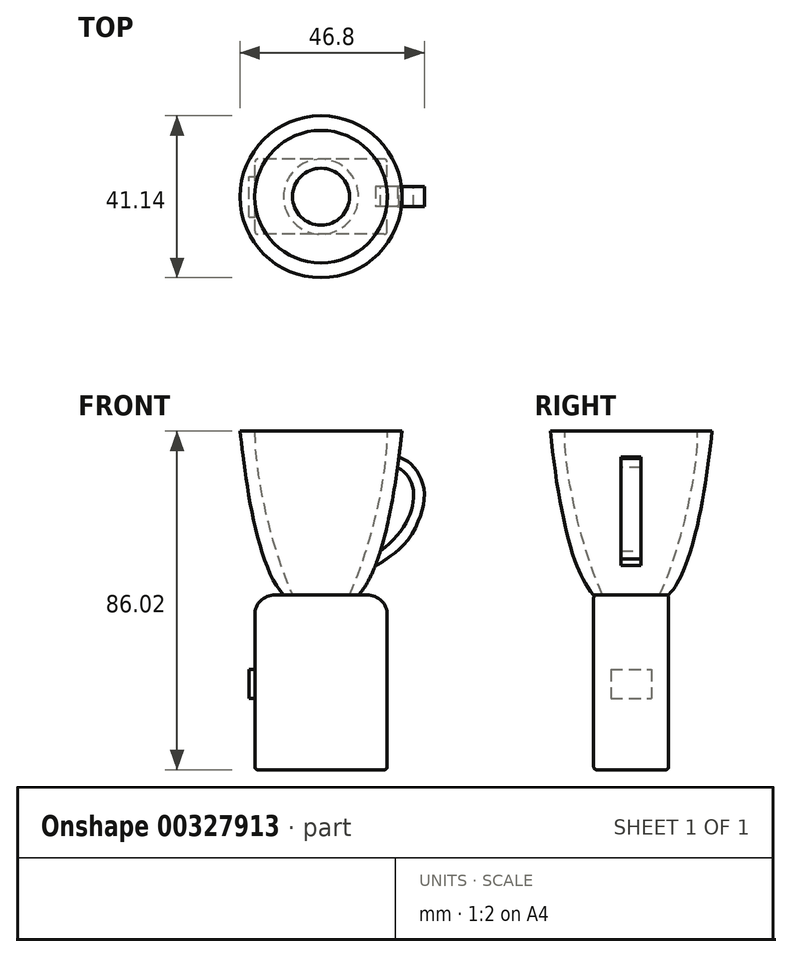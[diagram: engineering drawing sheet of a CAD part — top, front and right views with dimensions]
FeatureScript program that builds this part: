
annotation { "Feature Type Name" : "Feature", "Feature Type Description" : "" }
export const myFeature = defineFeature(function(context is Context, id is Id, definition is map)
    precondition{}
    {
        {
            var Q0;
            Q0=qCreatedBy(makeId("Front.planeOp"),FACE);
            var sketch = newSketch(context, id + "F0", { "sketchPlane" : qUnion([Q0])});
            skLineSegment(sketch, "E0.bottom", {"start": v(11.73, 0) * mm, "end": v(-11.73, 0) * mm});
            skLineSegment(sketch, "E0.top", {"start": v(16.81, -44.43) * mm, "end": v(-16.81, -44.43) * mm});
            skLineSegment(sketch, "E0.left", {"start": v(16.81, -5.08) * mm, "end": v(16.81, -44.43) * mm});
            skLineSegment(sketch, "E0.right", {"start": v(-16.81, -5.08) * mm, "end": v(-16.81, -44.43) * mm});
            skPoint(sketch, "E0.middle", {"position": v(0, -22.22) * mm});
            skLineSegment(sketch, "E1.top", {"start": v(20.57, 41.59) * mm, "end": v(-20.57, 41.59) * mm});
            skPoint(sketch, "E1.middle", {"position": v(0, 20.8) * mm});
            skFitSpline(sketch, "E2", {"points": [v(20.57, 41.59) * mm, v(9.52, 0) * mm], "startDerivative": vector(-3.41, -29.28) * mm, "endDerivative": vector(-21.77, -23.15) * mm});
            skFitSpline(sketch, "E3.MirrorCS", {"points": [v(-20.57, 41.59) * mm, v(-9.52, 0) * mm], "startDerivative": vector(3.41, -29.28) * mm, "endDerivative": vector(21.77, -23.15) * mm});
            skArc(sketch, "E4.filletArc", {"start": v(-11.73, 0) * mm, "mid": v(-15.33, -1.49) * mm, "end": v(-16.81, -5.08) * mm});
            skArc(sketch, "E5.filletArc", {"start": v(16.81, -5.08) * mm, "mid": v(15.33, -1.49) * mm, "end": v(11.73, 0) * mm});
            skLineSegment(sketch, "E6", {"start": v(20.05, 36.32) * mm, "end": v(19.95, 36.34) * mm});
            skPoint(sketch, "E7", {"position": v(19.44, 32.4) * mm});
            skPoint(sketch, "E8", {"position": v(15.09, 11.15) * mm});
            skFitSpline(sketch, "E9", {"points": [v(19.44, 32.4) * mm, v(15.09, 11.15) * mm], "startDerivative": vector(20, -10.29) * mm, "endDerivative": vector(-28.56, -21.1) * mm});
            skLineSegment(sketch, "E10", {"start": v(0, 0) * mm, "end": v(0, 41.59) * mm});
            skFitSpline(sketch, "E11", {"points": [v(-16.84, 41.59) * mm, v(-16.17, 32.06) * mm, v(-7.24, 0) * mm], "startDerivative": vector(-0.17, -23.5) * mm, "endDerivative": vector(23.63, -52.14) * mm});
            skFitSpline(sketch, "E12.0", {"points": [v(20.6, 34.67) * mm, v(21.69, 34.1) * mm, v(23.13, 33) * mm, v(24.53, 31.14) * mm, v(25.57, 29.08) * mm, v(26.2, 26.25) * mm, v(25.98, 22.68) * mm, v(24.89, 19.07) * mm, v(22.33, 14.33) * mm, v(19.2, 11.03) * mm, v(16.6, 9.1) * mm]});
            skLineSegment(sketch, "E13", {"start": v(20.6, 34.67) * mm, "end": v(19.78, 35.04) * mm});
            skFitSpline(sketch, "E14", {"points": [v(16.6, 9.1) * mm, v(13.8, 7.43) * mm], "startDerivative": vector(-2.48, -1.8) * mm, "endDerivative": vector(-3.15, -1.16) * mm});
            skSolve(sketch);
        }
        {
            var Q0;
            Q0=makeQuery(id+"F0.imprint","IMPRINT",FACE,{"disambiguationData":[TD([[makeQuery(id+"F0.imprint","IMPRINT",EDGE,{"derivedFrom":sQuery(id+"F0.wireOp",EDGE,"E0.top")}),-1.0]])]});
            extrude(context, id + "F1", {"entities" : qUnion([Q0]), "endBound" : BoundingType.SYMMETRIC, "depth" : 19.05 * mm});
        }
        {
            var Q0;
            Q0=makeQuery(id+"F1.opExtrude","CAP_EDGE",EDGE,{"disambiguationData":[OSD([sQuery(id+"F0.wireOp",EDGE,"E0.bottom")])],"isStart":false});
            var Q1;
            Q1=makeQuery(id+"F1.opExtrude","CAP_EDGE",EDGE,{"disambiguationData":[OSD([sQuery(id+"F0.wireOp",EDGE,"E0.left")])],"isStart":false});
            var Q2;
            Q2=makeQuery(id+"F1.opExtrude","CAP_EDGE",EDGE,{"disambiguationData":[OSD([sQuery(id+"F0.wireOp",EDGE,"E5.filletArc")])],"isStart":false});
            var Q3;
            Q3=makeQuery(id+"F1.opExtrude","CAP_EDGE",EDGE,{"disambiguationData":[OSD([sQuery(id+"F0.wireOp",EDGE,"E5.filletArc")])],"isStart":true});
            var Q4;
            Q4=makeQuery(id+"F1.opExtrude","CAP_EDGE",EDGE,{"disambiguationData":[OSD([sQuery(id+"F0.wireOp",EDGE,"E0.bottom")])],"isStart":true});
            var Q5;
            Q5=makeQuery(id+"F1.opExtrude","CAP_EDGE",EDGE,{"disambiguationData":[OSD([sQuery(id+"F0.wireOp",EDGE,"E0.left")])],"isStart":true});
            var Q6;
            Q6=makeQuery(id+"F1.opExtrude","CAP_EDGE",EDGE,{"disambiguationData":[OSD([sQuery(id+"F0.wireOp",EDGE,"E4.filletArc")])],"isStart":true});
            var Q7;
            Q7=makeQuery(id+"F1.opExtrude","CAP_FACE",FACE,{"disambiguationData":[OSD([sQuery(id+"F0.wireOp",EDGE,"E0.top"),sQuery(id+"F0.wireOp",EDGE,"E0.left"),sQuery(id+"F0.wireOp",EDGE,"E0.right"),sQuery(id+"F0.wireOp",EDGE,"E0.bottom"),sQuery(id+"F0.wireOp",EDGE,"E4.filletArc"),sQuery(id+"F0.wireOp",EDGE,"E5.filletArc")])],"isStart":true});
            var Q8;
            Q8=makeQuery(id+"F1.opExtrude","CAP_FACE",FACE,{"disambiguationData":[OSD([sQuery(id+"F0.wireOp",EDGE,"E0.top"),sQuery(id+"F0.wireOp",EDGE,"E0.left"),sQuery(id+"F0.wireOp",EDGE,"E0.right"),sQuery(id+"F0.wireOp",EDGE,"E0.bottom"),sQuery(id+"F0.wireOp",EDGE,"E4.filletArc"),sQuery(id+"F0.wireOp",EDGE,"E5.filletArc")])],"isStart":false});
            var Q9;
            Q9=makeQuery(id+"F1.opExtrude","SWEPT_FACE",FACE,{"disambiguationData":[OSD([sQuery(id+"F0.wireOp",EDGE,"E0.right")])]});
            var Q10;
            Q10=makeQuery(id+"F1.opExtrude","SWEPT_FACE",FACE,{"disambiguationData":[OSD([sQuery(id+"F0.wireOp",EDGE,"E0.left")])]});
            fillet(context, id + "F2", {"entities" : qUnion([Q0, Q1, Q2, Q3, Q4, Q5, Q6, Q7, Q8, Q9, Q10]), "radius" : 0.76 * mm, "tangentPropagation" : true, "allowEdgeOverflow" : false});
        }
        {
            var Q0;
            {var subQ0=sQuery(id+"F0.wireOp",EDGE,"E3.MirrorCS");Q0=makeQuery(id+"F0.imprint","IMPRINT",FACE,{"disambiguationData":[TD([[makeQuery(id+"F0.imprint","IMPRINT",EDGE,{"derivedFrom":subQ0}),1.0]])]});}
            var Q1;
            Q1=sQuery(id+"F0.wireOp",EDGE,"E10");
            revolve(context, id + "F3", {"entities" : qUnion([Q0]), "axis" : qUnion([Q1]), "revolveType" : RevolveType.FULL});
        }
        {
            var Q0;
            {var subQ0=sQuery(id+"F0.wireOp",EDGE,"E9");Q0=makeQuery(id+"F0.imprint","IMPRINT",FACE,{"disambiguationData":[TD([[makeQuery(id+"F0.imprint","IMPRINT",EDGE,{"derivedFrom":subQ0}),1.0]])]});}
            extrude(context, id + "F4", {"entities" : qUnion([Q0]), "operationType" : NewBodyOperationType.ADD, "endBound" : BoundingType.SYMMETRIC, "depth" : 5.08 * mm});
        }
        {
            var Q0;
            Q0=makeQuery(id+"F1.opExtrude","SWEPT_FACE",FACE,{"disambiguationData":[OSD([sQuery(id+"F0.wireOp",EDGE,"E0.right")])]});
            var sketch = newSketch(context, id + "F5", { "sketchPlane" : qUnion([Q0])});
            skLineSegment(sketch, "E15.bottom", {"start": v(5.18, -18.96) * mm, "end": v(-5.18, -18.96) * mm});
            skLineSegment(sketch, "E15.top", {"start": v(5.18, -26.36) * mm, "end": v(-5.18, -26.36) * mm});
            skLineSegment(sketch, "E15.left", {"start": v(5.18, -18.96) * mm, "end": v(5.18, -26.36) * mm});
            skLineSegment(sketch, "E15.right", {"start": v(-5.18, -18.96) * mm, "end": v(-5.18, -26.36) * mm});
            skPoint(sketch, "E15.middle", {"position": v(0, -22.66) * mm});
            skSolve(sketch);
        }
        {
            var Q0;
            Q0=makeQuery(id+"F5.imprint","IMPRINT",FACE,{"disambiguationData":[TD([[makeQuery(id+"F5.imprint","IMPRINT",EDGE,{"derivedFrom":sQuery(id+"F5.wireOp",EDGE,"E15.bottom")}),1.0]])]});
            extrude(context, id + "F6", {"entities" : qUnion([Q0]), "operationType" : NewBodyOperationType.ADD, "depth" : 1.52 * mm});
        }
    });
